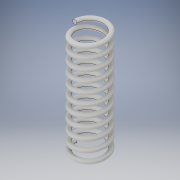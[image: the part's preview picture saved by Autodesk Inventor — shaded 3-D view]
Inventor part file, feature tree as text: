
AUTODESK INVENTOR PART (.ipt)
format: ipt  version: 2018 (Build 220112000, 112)  size: 540,672 bytes
history: native  units: in
note: dims shown in document units (in); Inventor stores cm internally (conversion verified against a paired STEP export)
features: helix x1, sketch x1
ambient origin geometry x8: Origin, YZ Plane, XZ Plane, XY Plane, X Axis, Y Axis, Z Axis, Center Point
bodies: Solid1 (feature_tree)
feature tree (2):
  helix  "Coil1"  [1 undecoded]
  sketch  "Sketch1"  dims[d1=0.16in d2=1.0in d3=0.9449in d4=3.937in d5=0.0in d6=90.0deg d7=90.0deg d8=90.0deg d9=90.0deg]
note: 1 required parameter value undecoded (feature->parameter linkage not recoverable at this tier; creation-order binding heuristic only, values carry confidence <= 0.55)
